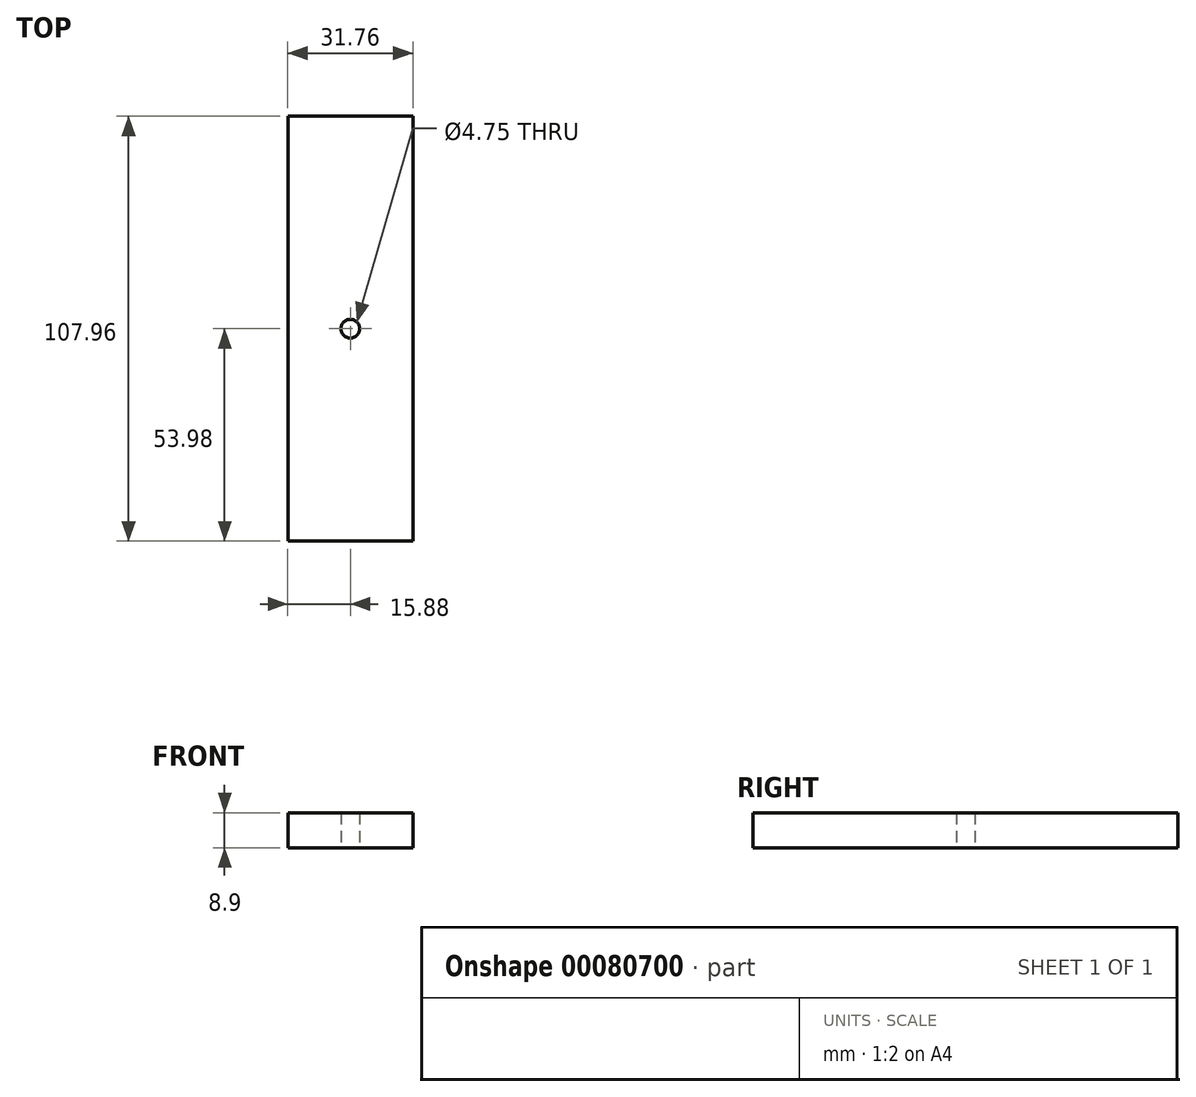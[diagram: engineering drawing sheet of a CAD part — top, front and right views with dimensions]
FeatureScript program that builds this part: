
annotation { "Feature Type Name" : "Feature", "Feature Type Description" : "" }
export const myFeature = defineFeature(function(context is Context, id is Id, definition is map)
    precondition{}
    {
        {
            var Q0;
            Q0=qCreatedBy(makeId("Top.planeOp"),FACE);
            var sketch = newSketch(context, id + "F0", { "sketchPlane" : qUnion([Q0])});
            skLineSegment(sketch, "E0.bottom", {"start": v(15.88, -53.98) * mm, "end": v(-15.87, -53.98) * mm});
            skLineSegment(sketch, "E0.top", {"start": v(15.87, 53.97) * mm, "end": v(-15.88, 53.97) * mm});
            skLineSegment(sketch, "E0.left", {"start": v(15.88, -53.98) * mm, "end": v(15.87, 53.97) * mm});
            skLineSegment(sketch, "E0.right", {"start": v(-15.87, -53.98) * mm, "end": v(-15.88, 53.97) * mm});
            skPoint(sketch, "E0.middle", {"position": v(0, 0) * mm});
            skCircle(sketch, "E1", {"center": v(0, 0) * mm, "radius": 2.37 * mm});
            skSolve(sketch);
        }
        {
            var Q0;
            Q0=makeQuery(id+"F0.imprint","IMPRINT",FACE,{"disambiguationData":[TD([[makeQuery(id+"F0.imprint","IMPRINT",EDGE,{"derivedFrom":sQuery(id+"F0.wireOp",EDGE,"E0.bottom")}),-1.0]])]});
            extrude(context, id + "F1", {"entities" : qUnion([Q0]), "endBound" : BoundingType.SYMMETRIC, "depth" : 8.9 * mm});
        }
    });
